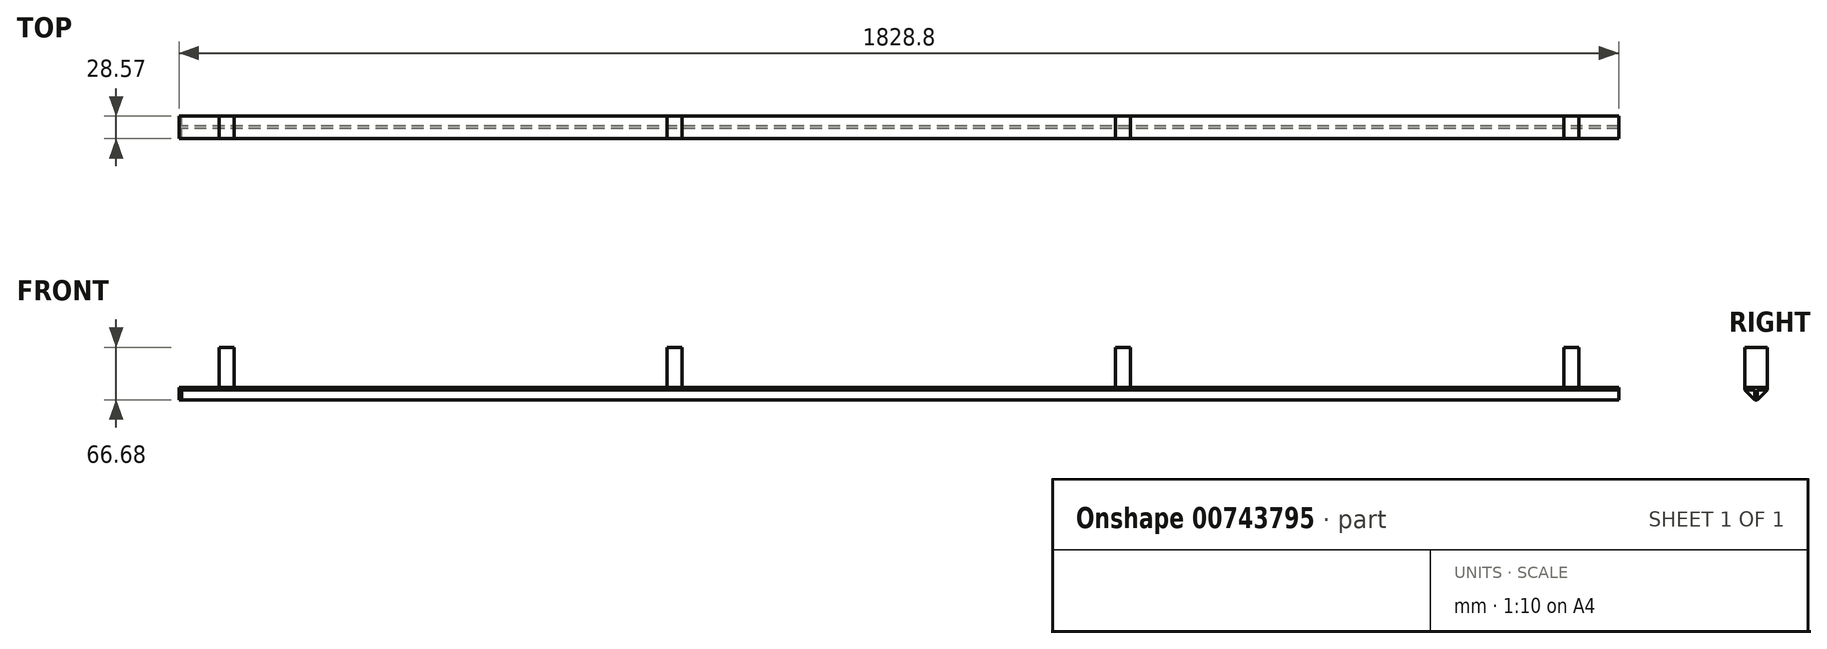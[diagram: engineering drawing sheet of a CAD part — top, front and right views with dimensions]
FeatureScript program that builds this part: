
annotation { "Feature Type Name" : "Feature", "Feature Type Description" : "" }
export const myFeature = defineFeature(function(context is Context, id is Id, definition is map)
    precondition{}
    {
        {
            var Q0;
            Q0=qCreatedBy(makeId("Top.planeOp"),FACE);
            var sketch = newSketch(context, id + "F0", { "sketchPlane" : qUnion([Q0])});
            skLineSegment(sketch, "E0.bottom", {"start": v(0, 0) * mm, "end": v(-1828.8, 0) * mm});
            skLineSegment(sketch, "E0.top", {"start": v(0, 28.57) * mm, "end": v(-1828.8, 28.57) * mm});
            skLineSegment(sketch, "E0.left", {"start": v(0, 0) * mm, "end": v(0, 28.57) * mm});
            skLineSegment(sketch, "E0.right", {"start": v(-1828.8, 0) * mm, "end": v(-1828.8, 28.57) * mm});
            skSolve(sketch);
        }
        {
            var Q0;
            Q0=qSketchRegion(id+"F0",true);
            extrude(context, id + "F1", {"entities" : qUnion([Q0]), "depth" : 3.17 * mm, "offsetDistance" : 25.4 * mm});
        }
        {
            var Q0;
            Q0=makeQuery(id+"F1.opExtrude","CAP_FACE",FACE,{"disambiguationData":[OSD([sQuery(id+"F0.wireOp",EDGE,"E0.bottom"),sQuery(id+"F0.wireOp",EDGE,"E0.top"),sQuery(id+"F0.wireOp",EDGE,"E0.left"),sQuery(id+"F0.wireOp",EDGE,"E0.right")])],"isStart":false});
            var sketch = newSketch(context, id + "F2", { "sketchPlane" : qUnion([Q0])});
            skCircle(sketch, "E1", {"center": v(-50.8, 14.29) * mm, "radius": 4.76 * mm});
            skSolve(sketch);
        }
        {
            var Q0;
            Q0=makeQuery(id+"F2.imprint","IMPRINT",FACE,{"disambiguationData":[TD([[makeQuery(id+"F2.imprint","IMPRINT",EDGE,{"derivedFrom":sQuery(id+"F2.wireOp",EDGE,"E1")}),-1.0]])]});
            var sketch = newSketch(context, id + "F3", { "sketchPlane" : qUnion([Q0])});
            skCircle(sketch, "E2", {"center": v(-1768.48, 14.29) * mm, "radius": 4.76 * mm});
            skCircle(sketch, "E3.1.0.0", {"center": v(-1199.08, 14.29) * mm, "radius": 4.76 * mm});
            skCircle(sketch, "E3.2.0.0", {"center": v(-629.7, 14.29) * mm, "radius": 4.76 * mm});
            skCircle(sketch, "E3.3.0.0", {"center": v(-60.3, 14.29) * mm, "radius": 4.76 * mm});
            skLineSegment(sketch, "E3.direction1", {"start": v(-1768.48, 14.29) * mm, "end": v(-1199.08, 14.29) * mm, "construction": true});
            skSolve(sketch);
        }
        {
            var Q0;
            Q0=makeQuery(id+"F2.imprint","IMPRINT",FACE,{"disambiguationData":[TD([[makeQuery(id+"F2.imprint","IMPRINT",EDGE,{"derivedFrom":sQuery(id+"F2.wireOp",EDGE,"E1")}),-1.0]])]});
            var sketch = newSketch(context, id + "F4", { "sketchPlane" : qUnion([Q0])});
            skLineSegment(sketch, "E4.bottom", {"start": v(-1778, 28.58) * mm, "end": v(-1758.95, 28.58) * mm});
            skLineSegment(sketch, "E4.top", {"start": v(-1778, 0) * mm, "end": v(-1758.95, 0) * mm});
            skLineSegment(sketch, "E4.left", {"start": v(-1778, 28.58) * mm, "end": v(-1778, 0) * mm});
            skLineSegment(sketch, "E4.right", {"start": v(-1758.95, 28.58) * mm, "end": v(-1758.95, 0) * mm});
            skLineSegment(sketch, "E5.1.0.0", {"start": v(-1208.62, 28.58) * mm, "end": v(-1208.62, 0) * mm});
            skLineSegment(sketch, "E5.1.0.1", {"start": v(-1208.62, 28.58) * mm, "end": v(-1189.57, 28.58) * mm});
            skLineSegment(sketch, "E5.1.0.2", {"start": v(-1208.62, 0) * mm, "end": v(-1189.57, 0) * mm});
            skLineSegment(sketch, "E5.1.0.3", {"start": v(-1189.57, 28.58) * mm, "end": v(-1189.57, 0) * mm});
            skLineSegment(sketch, "E5.2.0.0", {"start": v(-639.23, 28.58) * mm, "end": v(-639.23, 0) * mm});
            skLineSegment(sketch, "E5.2.0.1", {"start": v(-639.23, 28.58) * mm, "end": v(-620.18, 28.58) * mm});
            skLineSegment(sketch, "E5.2.0.2", {"start": v(-639.23, 0) * mm, "end": v(-620.18, 0) * mm});
            skLineSegment(sketch, "E5.2.0.3", {"start": v(-620.18, 28.58) * mm, "end": v(-620.18, 0) * mm});
            skLineSegment(sketch, "E5.3.0.0", {"start": v(-69.85, 28.58) * mm, "end": v(-69.85, 0) * mm});
            skLineSegment(sketch, "E5.3.0.1", {"start": v(-69.85, 28.58) * mm, "end": v(-50.8, 28.58) * mm});
            skLineSegment(sketch, "E5.3.0.2", {"start": v(-69.85, 0) * mm, "end": v(-50.8, 0) * mm});
            skLineSegment(sketch, "E5.3.0.3", {"start": v(-50.8, 28.58) * mm, "end": v(-50.8, 0) * mm});
            skLineSegment(sketch, "E5.direction1", {"start": v(-1787.53, 0) * mm, "end": v(-1218.14, 0) * mm, "construction": true});
            skLineSegment(sketch, "E6.1.0.2", {"start": v(-1218.14, 0) * mm, "end": v(-648.76, 0) * mm, "construction": true});
            skLineSegment(sketch, "E6.2.0.2", {"start": v(-648.76, 0) * mm, "end": v(-79.38, 0) * mm, "construction": true});
            skLineSegment(sketch, "E6.3.0.2", {"start": v(-79.38, 0) * mm, "end": v(490, 0) * mm, "construction": true});
            skLineSegment(sketch, "E6.direction1", {"start": v(-1778, 0) * mm, "end": v(-1208.62, 0) * mm, "construction": true});
            skSolve(sketch);
        }
        {
            var Q0;
            Q0=qSketchRegion(id+"F4",true);
            extrude(context, id + "F5", {"entities" : qUnion([Q0]), "depth" : 50.8 * mm, "offsetDistance" : 25.4 * mm});
        }
        {
            var Q0;
            Q0=makeQuery(id+"F1.opExtrude","CAP_FACE",FACE,{"disambiguationData":[OSD([sQuery(id+"F0.wireOp",EDGE,"E0.bottom"),sQuery(id+"F0.wireOp",EDGE,"E0.top"),sQuery(id+"F0.wireOp",EDGE,"E0.left"),sQuery(id+"F0.wireOp",EDGE,"E0.right")])],"isStart":true});
            var sketch = newSketch(context, id + "F6", { "sketchPlane" : qUnion([Q0])});
            skLineSegment(sketch, "E7.bottom", {"start": v(0, -12.7) * mm, "end": v(-1828.8, -12.7) * mm});
            skLineSegment(sketch, "E7.top", {"start": v(0, -15.87) * mm, "end": v(-1828.8, -15.88) * mm});
            skLineSegment(sketch, "E7.left", {"start": v(0, -12.7) * mm, "end": v(0, -15.87) * mm});
            skLineSegment(sketch, "E7.right", {"start": v(-1828.8, -12.7) * mm, "end": v(-1828.8, -15.88) * mm});
            skSolve(sketch);
        }
        {
            var Q0;
            Q0 = qSketchRegion(id + "F6", true);
            extrude(context, id + "F7", {"entities" : qUnion([Q0]), "operationType" : NewBodyOperationType.ADD, "depth" : 12.7 * mm, "offsetDistance" : 25.4 * mm});
        }
        {
            var Q0;
            Q0=makeQuery(id+"F7.boolean.opBoolean","MERGE",FACE,{"derivedFrom":[makeQuery(id+"F1.opExtrude","SWEPT_FACE",FACE,{"disambiguationData":[OSD([sQuery(id+"F0.wireOp",EDGE,"E0.right")])]}),makeQuery(id+"F7.opExtrude","SWEPT_FACE",FACE,{"disambiguationData":[OSD([sQuery(id+"F6.wireOp",EDGE,"E7.right")])]})]});
            var sketch = newSketch(context, id + "F8", { "sketchPlane" : qUnion([Q0])});
            skLineSegment(sketch, "E8", {"start": v(0, 0) * mm, "end": v(-12.7, -12.7) * mm});
            skLineSegment(sketch, "E9", {"start": v(-12.7, -12.7) * mm, "end": v(-15.88, -12.7) * mm});
            skLineSegment(sketch, "E10", {"start": v(-15.88, -12.7) * mm, "end": v(-28.57, 0) * mm});
            skSolve(sketch);
        }
        {
            var Q0;
            Q0 = qSketchRegion(id + "F8", true);
            var Q1;
            Q1=makeQuery(id+"F8.imprint","IMPRINT",FACE,{"disambiguationData":[TD([[makeQuery(id+"F8.imprint","IMPRINT",EDGE,{"derivedFrom":sQuery(id+"F8.wireOp",EDGE,"E8")}),-1.0]])]});
            var Q2;
            Q2=makeQuery(id+"F8.imprint","IMPRINT",FACE,{"disambiguationData":[TD([[makeQuery(id+"F8.imprint","IMPRINT",EDGE,{"derivedFrom":sQuery(id+"F8.wireOp",EDGE,"E10")}),-1.0]])]});
            extrude(context, id + "F9", {"entities" : qUnion([Q0, Q1, Q2]), "oppositeDirection" : true, "depth" : 3.17 * mm, "offsetDistance" : 25.4 * mm});
        }
        {
            var Q0;
            Q0 = qSketchRegion(id + "F8", true);
            var Q1;
            Q1=makeQuery(id+"F8.imprint","IMPRINT",FACE,{"disambiguationData":[TD([[makeQuery(id+"F8.imprint","IMPRINT",EDGE,{"derivedFrom":sQuery(id+"F8.wireOp",EDGE,"E8")}),-1.0]])]});
            var Q2;
            Q2=makeQuery(id+"F8.imprint","IMPRINT",FACE,{"disambiguationData":[TD([[makeQuery(id+"F8.imprint","IMPRINT",EDGE,{"derivedFrom":sQuery(id+"F8.wireOp",EDGE,"E10")}),-1.0]])]});
            extrude(context, id + "F10", {"entities" : qUnion([Q0, Q1, Q2]), "operationType" : NewBodyOperationType.ADD, "oppositeDirection" : true, "depth" : 3.17 * mm, "offsetDistance" : 25.4 * mm});
        }
    });
